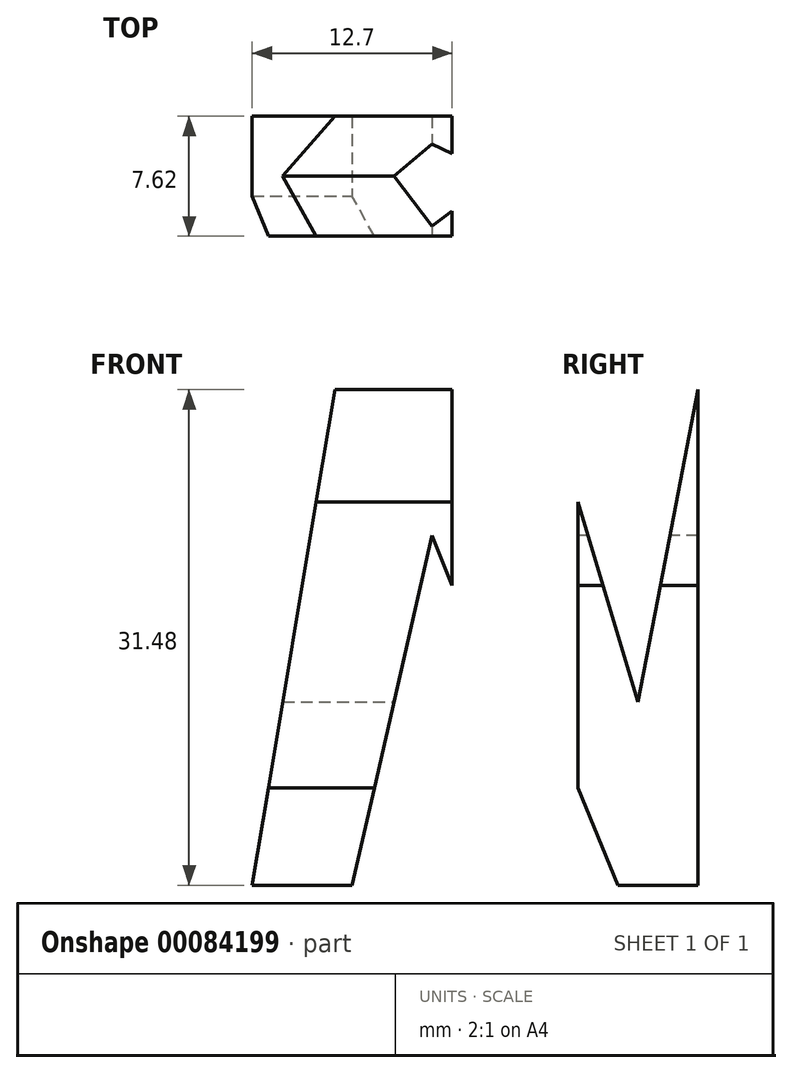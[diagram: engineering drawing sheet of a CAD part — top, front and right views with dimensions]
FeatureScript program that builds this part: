
annotation { "Feature Type Name" : "Feature", "Feature Type Description" : "" }
export const myFeature = defineFeature(function(context is Context, id is Id, definition is map)
    precondition{}
    {
        {
            var Q0;
            Q0=qCreatedBy(makeId("Front.planeOp"),FACE);
            var sketch = newSketch(context, id + "F0", { "sketchPlane" : qUnion([Q0])});
            skLineSegment(sketch, "E0", {"start": v(0, 0) * mm, "end": v(0, 38.1) * mm});
            skLineSegment(sketch, "E1", {"start": v(0, 0) * mm, "end": v(38.1, 0) * mm});
            skLineSegment(sketch, "E2", {"start": v(38.1, 0) * mm, "end": v(38.1, 38.1) * mm});
            skLineSegment(sketch, "E3", {"start": v(38.1, 38.1) * mm, "end": v(0, 38.1) * mm});
            skSolve(sketch);
        }
        {
            var Q0;
            Q0=makeQuery(id+"F0.imprint","IMPRINT",FACE,{"disambiguationData":[TD([[makeQuery(id+"F0.imprint","IMPRINT",EDGE,{"derivedFrom":sQuery(id+"F0.wireOp",EDGE,"E0")}),-1.0]])]});
            extrude(context, id + "F1", {"entities" : qUnion([Q0]), "depth" : 38.1 * mm});
        }
        {
            var Q0;
            Q0=qCreatedBy(makeId("Front.planeOp"),FACE);
            cPlane(context, id + "F2", {"entities" : qUnion([Q0]), "cplaneType" : CPlaneType.OFFSET, "offset" : 38.1 * mm, "width" : 152.4 * mm, "height" : 152.4 * mm});
        }
        {
            var Q0;
            Q0=qCreatedBy(makeId("Top.planeOp"),FACE);
            cPlane(context, id + "F3", {"entities" : qUnion([Q0]), "cplaneType" : CPlaneType.OFFSET, "offset" : 38.1 * mm, "width" : 152.4 * mm, "height" : 152.4 * mm});
        }
        {
            var Q0;
            Q0=makeQuery(id+"F1.opExtrude","SWEPT_FACE",FACE,{"disambiguationData":[OSD([sQuery(id+"F0.wireOp",EDGE,"E2")])]});
            var sketch = newSketch(context, id + "F4", { "sketchPlane" : qUnion([Q0])});
            skLineSegment(sketch, "E4", {"start": v(-38.1, 38.1) * mm, "end": v(-31.75, 0) * mm});
            skLineSegment(sketch, "E5", {"start": v(-31.75, 0) * mm, "end": v(-25.4, 0) * mm});
            skLineSegment(sketch, "E6", {"start": v(-25.4, 0) * mm, "end": v(-19.21, 15.88) * mm});
            skLineSegment(sketch, "E7", {"start": v(-19.21, 15.88) * mm, "end": v(-12.7, 0) * mm});
            skLineSegment(sketch, "E8", {"start": v(-12.7, 0) * mm, "end": v(-6.35, 0) * mm});
            skLineSegment(sketch, "E9", {"start": v(-6.35, 0) * mm, "end": v(0, 38.1) * mm});
            skLineSegment(sketch, "E10", {"start": v(0, 38.1) * mm, "end": v(-6.35, 38.1) * mm});
            skLineSegment(sketch, "E11", {"start": v(-6.35, 38.1) * mm, "end": v(-11.43, 11.64) * mm});
            skLineSegment(sketch, "E12", {"start": v(-11.43, 11.64) * mm, "end": v(-16.51, 28.57) * mm});
            skLineSegment(sketch, "E13", {"start": v(-16.51, 28.57) * mm, "end": v(-21.6, 28.57) * mm});
            skLineSegment(sketch, "E14", {"start": v(-21.6, 28.57) * mm, "end": v(-26.67, 11.64) * mm});
            skLineSegment(sketch, "E15", {"start": v(-26.67, 11.64) * mm, "end": v(-31.75, 38.1) * mm});
            skLineSegment(sketch, "E16", {"start": v(-38.1, 38.1) * mm, "end": v(-38.1, 0) * mm});
            skLineSegment(sketch, "E17", {"start": v(-38.1, 0) * mm, "end": v(0, 0) * mm});
            skLineSegment(sketch, "E18", {"start": v(0, 0) * mm, "end": v(0, 38.1) * mm});
            skLineSegment(sketch, "E19", {"start": v(-38.1, 38.1) * mm, "end": v(0, 38.1) * mm});
            skLineSegment(sketch, "E20", {"start": v(-38.1, 38.1) * mm, "end": v(-31.75, 38.1) * mm});
            skSolve(sketch);
        }
        {
            var Q0;
            {var subQ1=sQuery(id+"F4.wireOp",EDGE,"E11");Q0=makeQuery(id+"F4.imprint","IMPRINT",FACE,{"disambiguationData":[TD([[makeQuery(id+"F4.imprint","IMPRINT",EDGE,{"derivedFrom":subQ1}),-1.0]])]});}
            var Q1;
            {var subQ0=sQuery(id+"F4.wireOp",EDGE,"E4");Q1=makeQuery(id+"F4.imprint","IMPRINT",FACE,{"disambiguationData":[TD([[makeQuery(id+"F4.imprint","IMPRINT",EDGE,{"derivedFrom":subQ0}),-1.0]])]});}
            var Q2;
            {var subQ0=sQuery(id+"F4.wireOp",EDGE,"E6");Q2=makeQuery(id+"F4.imprint","IMPRINT",FACE,{"disambiguationData":[TD([[makeQuery(id+"F4.imprint","IMPRINT",EDGE,{"derivedFrom":subQ0}),-1.0]])]});}
            var Q3;
            {var subQ0=sQuery(id+"F4.wireOp",EDGE,"E9");Q3=makeQuery(id+"F4.imprint","IMPRINT",FACE,{"disambiguationData":[TD([[makeQuery(id+"F4.imprint","IMPRINT",EDGE,{"derivedFrom":subQ0}),-1.0]])]});}
            extrude(context, id + "F5", {"entities" : qUnion([Q0, Q1, Q2, Q3]), "operationType" : NewBodyOperationType.REMOVE, "oppositeDirection" : true, "depth" : 25.4 * mm});
        }
        {
            var Q0;
            Q0=qCreatedBy(id+"F2.planeOp",FACE);
            var sketch = newSketch(context, id + "F6", { "sketchPlane" : qUnion([Q0])});
            skLineSegment(sketch, "E21", {"start": v(0, 0) * mm, "end": v(6.35, 38.1) * mm});
            skLineSegment(sketch, "E22", {"start": v(6.35, 38.1) * mm, "end": v(12.7, 38.1) * mm});
            skLineSegment(sketch, "E23", {"start": v(12.7, 38.1) * mm, "end": v(19.05, 22.22) * mm});
            skLineSegment(sketch, "E24", {"start": v(19.05, 22.22) * mm, "end": v(25.4, 38.1) * mm});
            skLineSegment(sketch, "E25", {"start": v(31.75, 0) * mm, "end": v(26.67, 22.23) * mm});
            skLineSegment(sketch, "E26", {"start": v(26.67, 22.23) * mm, "end": v(21.59, 9.52) * mm});
            skLineSegment(sketch, "E27", {"start": v(21.6, 9.53) * mm, "end": v(16.51, 9.53) * mm});
            skLineSegment(sketch, "E28", {"start": v(16.51, 9.53) * mm, "end": v(11.43, 22.23) * mm});
            skLineSegment(sketch, "E29", {"start": v(6.35, 0) * mm, "end": v(0, 0) * mm});
            skLineSegment(sketch, "E30", {"start": v(38.1, 0) * mm, "end": v(31.75, 0) * mm});
            skLineSegment(sketch, "E31", {"start": v(11.43, 22.23) * mm, "end": v(6.35, 0) * mm});
            skLineSegment(sketch, "E32", {"start": v(25.4, 38.1) * mm, "end": v(31.75, 38.1) * mm});
            skLineSegment(sketch, "E33", {"start": v(31.75, 38.1) * mm, "end": v(38.1, 0) * mm});
            skLineSegment(sketch, "E34", {"start": v(12.7, 38.1) * mm, "end": v(25.4, 38.1) * mm});
            skLineSegment(sketch, "E35", {"start": v(6.35, 0) * mm, "end": v(31.75, 0) * mm});
            skLineSegment(sketch, "E36", {"start": v(6.35, 38.1) * mm, "end": v(0, 38.1) * mm});
            skLineSegment(sketch, "E37", {"start": v(0, 38.1) * mm, "end": v(0, 0) * mm});
            skLineSegment(sketch, "E38", {"start": v(31.75, 38.1) * mm, "end": v(38, 38.1) * mm});
            skLineSegment(sketch, "E39", {"start": v(38, 38.1) * mm, "end": v(38.1, 0) * mm});
            skSolve(sketch);
        }
        {
            var Q0;
            Q0=makeQuery(id+"F5.boolean.opBoolean","COPY",FACE,{"derivedFrom":makeQuery(id+"F5.opExtrude","CAP_FACE",FACE,{"disambiguationData":[OSD([sQuery(id+"F4.wireOp",EDGE,"E11"),sQuery(id+"F4.wireOp",EDGE,"E12"),sQuery(id+"F4.wireOp",EDGE,"E13"),sQuery(id+"F4.wireOp",EDGE,"E14"),sQuery(id+"F4.wireOp",EDGE,"E15"),sQuery(id+"F4.wireOp",EDGE,"E19")])],"isStart":false})});
            var Q1;
            Q1=makeQuery(id+"F5.boolean.opBoolean","COPY",FACE,{"derivedFrom":makeQuery(id+"F5.opExtrude","CAP_FACE",FACE,{"disambiguationData":[OSD([sQuery(id+"F4.wireOp",EDGE,"E4"),sQuery(id+"F4.wireOp",EDGE,"E16"),sQuery(id+"F4.wireOp",EDGE,"E17")])],"isStart":false})});
            var Q2;
            Q2=makeQuery(id+"F5.boolean.opBoolean","COPY",FACE,{"derivedFrom":makeQuery(id+"F5.opExtrude","CAP_FACE",FACE,{"disambiguationData":[OSD([sQuery(id+"F4.wireOp",EDGE,"E6"),sQuery(id+"F4.wireOp",EDGE,"E7"),sQuery(id+"F4.wireOp",EDGE,"E17")])],"isStart":false})});
            var Q3;
            Q3=makeQuery(id+"F5.boolean.opBoolean","COPY",FACE,{"derivedFrom":makeQuery(id+"F5.opExtrude","CAP_FACE",FACE,{"disambiguationData":[OSD([sQuery(id+"F4.wireOp",EDGE,"E9"),sQuery(id+"F4.wireOp",EDGE,"E17"),sQuery(id+"F4.wireOp",EDGE,"E18")])],"isStart":false})});
            extrude(context, id + "F7", {"entities" : qUnion([Q0, Q1, Q2, Q3]), "operationType" : NewBodyOperationType.REMOVE, "oppositeDirection" : true, "depth" : 38.1 * mm});
        }
        {
            var Q0;
            Q0=makeQuery(id+"F6.imprint","IMPRINT",FACE,{"disambiguationData":[TD([[makeQuery(id+"F6.imprint","IMPRINT",EDGE,{"derivedFrom":sQuery(id+"F6.wireOp",EDGE,"E21")}),1.0]])]});
            var Q1;
            Q1=makeQuery(id+"F6.imprint","IMPRINT",FACE,{"disambiguationData":[TD([[makeQuery(id+"F6.imprint","IMPRINT",EDGE,{"derivedFrom":sQuery(id+"F6.wireOp",EDGE,"E23")}),1.0]])]});
            var Q2;
            Q2=makeQuery(id+"F6.imprint","IMPRINT",FACE,{"disambiguationData":[TD([[makeQuery(id+"F6.imprint","IMPRINT",EDGE,{"derivedFrom":sQuery(id+"F6.wireOp",EDGE,"E25")}),1.0]])]});
            var Q3;
            Q3=makeQuery(id+"F6.imprint","IMPRINT",FACE,{"disambiguationData":[TD([[makeQuery(id+"F6.imprint","IMPRINT",EDGE,{"derivedFrom":sQuery(id+"F6.wireOp",EDGE,"E33")}),1.0]])]});
            extrude(context, id + "F8", {"entities" : qUnion([Q0, Q1, Q2, Q3]), "operationType" : NewBodyOperationType.REMOVE, "oppositeDirection" : true, "depth" : 38.1 * mm});
        }
        {
            var Q0;
            Q0=qCreatedBy(id+"F3.planeOp",FACE);
            var sketch = newSketch(context, id + "F9", { "sketchPlane" : qUnion([Q0])});
            skLineSegment(sketch, "E40", {"start": v(0, 0) * mm, "end": v(38.1, 0) * mm});
            skLineSegment(sketch, "E41", {"start": v(38.1, 0) * mm, "end": v(38.1, -38.1) * mm});
            skLineSegment(sketch, "E42", {"start": v(38.1, -38.1) * mm, "end": v(0, -38.1) * mm});
            skLineSegment(sketch, "E43", {"start": v(0, -38.1) * mm, "end": v(0, 0) * mm});
            skLineSegment(sketch, "E44", {"start": v(38.1, -7.62) * mm, "end": v(12.7, -7.62) * mm});
            skLineSegment(sketch, "E45", {"start": v(12.7, -7.62) * mm, "end": v(12.7, -15.24) * mm});
            skLineSegment(sketch, "E46", {"start": v(12.7, -15.24) * mm, "end": v(38.1, -15.24) * mm});
            skLineSegment(sketch, "E47", {"start": v(0, -22.86) * mm, "end": v(25.4, -22.86) * mm});
            skPoint(sketch, "E47.endSnap0", {"position": v(0, -22.86) * mm});
            skLineSegment(sketch, "E48", {"start": v(25.4, -22.86) * mm, "end": v(25.4, -30.48) * mm});
            skLineSegment(sketch, "E49", {"start": v(25.4, -30.48) * mm, "end": v(0, -30.48) * mm});
            skSolve(sketch);
        }
        {
            var Q0;
            {var subQ0=sQuery(id+"F9.wireOp",EDGE,"E44");Q0=makeQuery(id+"F9.imprint","IMPRINT",FACE,{"disambiguationData":[TD([[makeQuery(id+"F9.imprint","IMPRINT",EDGE,{"derivedFrom":subQ0}),1.0]])]});}
            var Q1;
            {var subQ0=sQuery(id+"F9.wireOp",EDGE,"E47");Q1=makeQuery(id+"F9.imprint","IMPRINT",FACE,{"disambiguationData":[TD([[makeQuery(id+"F9.imprint","IMPRINT",EDGE,{"derivedFrom":subQ0}),-1.0]])]});}
            extrude(context, id + "F10", {"entities" : qUnion([Q0, Q1]), "operationType" : NewBodyOperationType.REMOVE, "oppositeDirection" : true, "depth" : 38.1 * mm});
        }
        {
            var Q0;
            Q0=makeQuery(id+"F1.opExtrude","SWEPT_FACE",FACE,{"disambiguationData":[OSD([sQuery(id+"F0.wireOp",EDGE,"E2")])]});
            extrude(context, id + "F11", {"entities" : qUnion([Q0]), "operationType" : NewBodyOperationType.REMOVE, "oppositeDirection" : true, "depth" : 38.1 * mm});
        }
    });
